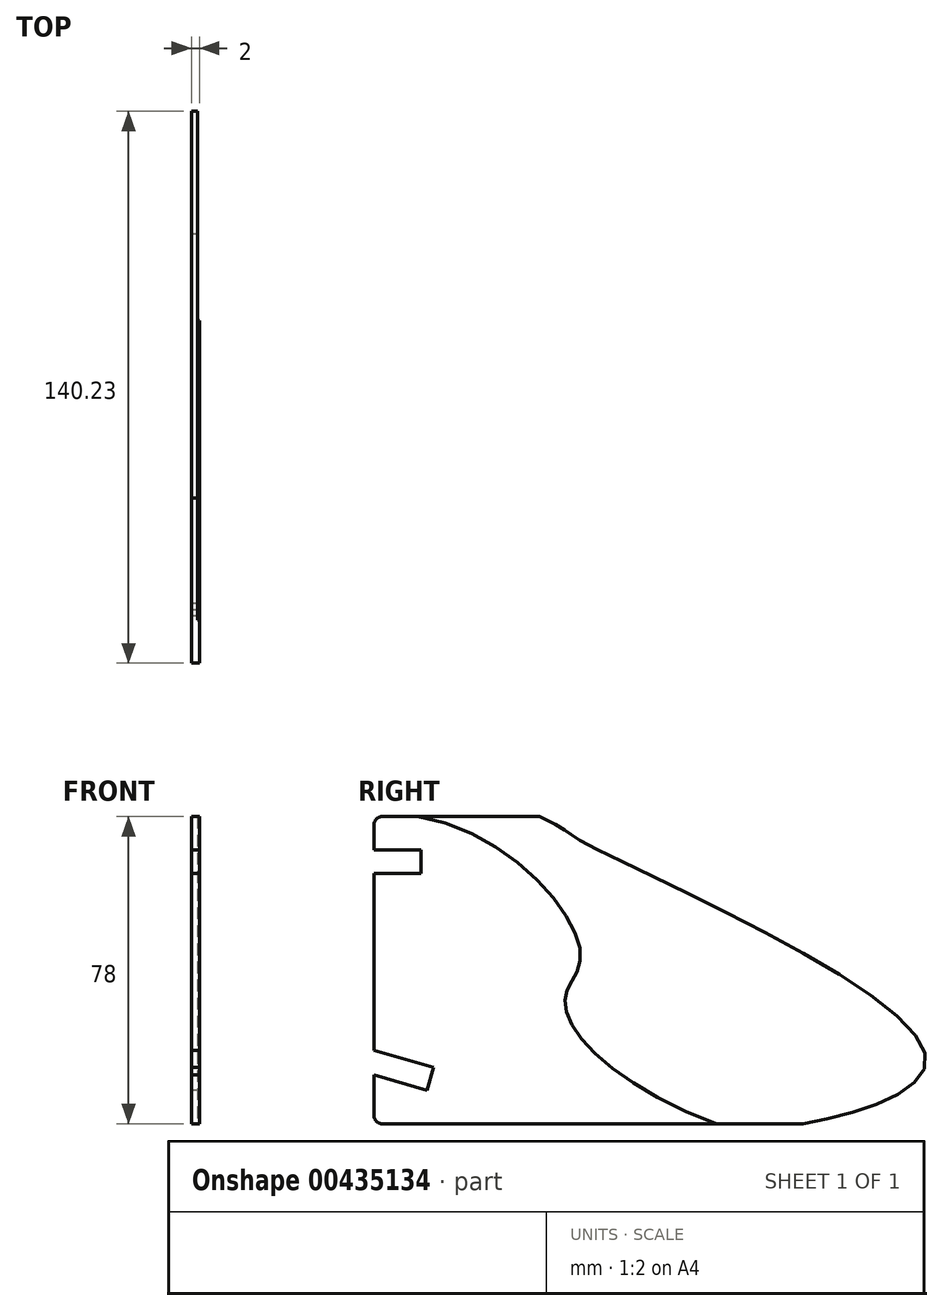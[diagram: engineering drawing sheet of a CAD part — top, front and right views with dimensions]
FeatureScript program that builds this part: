
annotation { "Feature Type Name" : "Feature", "Feature Type Description" : "" }
export const myFeature = defineFeature(function(context is Context, id is Id, definition is map)
    precondition{}
    {
        {
            var Q0;
            Q0=qCreatedBy(makeId("Right.planeOp"),FACE);
            var sketch = newSketch(context, id + "F0", { "sketchPlane" : qUnion([Q0])});
            skLineSegment(sketch, "E0", {"start": v(2, 78) * mm, "end": v(42, 78) * mm});
            skLineSegment(sketch, "E1", {"start": v(2, 0) * mm, "end": v(109, 0) * mm});
            skLineSegment(sketch, "E2", {"start": v(0, 76) * mm, "end": v(0, 69.6) * mm});
            skLineSegment(sketch, "E3", {"start": v(0, 69.6) * mm, "end": v(12, 69.6) * mm});
            skLineSegment(sketch, "E4", {"start": v(12, 69.6) * mm, "end": v(12, 63.6) * mm});
            skLineSegment(sketch, "E5", {"start": v(12, 63.6) * mm, "end": v(0, 63.6) * mm});
            skLineSegment(sketch, "E6", {"start": v(0, 63.6) * mm, "end": v(0, 18.6) * mm});
            skLineSegment(sketch, "E7", {"start": v(0, 18.6) * mm, "end": v(15.11, 14.26) * mm});
            skLineSegment(sketch, "E8", {"start": v(15.11, 14.26) * mm, "end": v(13.46, 8.5) * mm});
            skLineSegment(sketch, "E9", {"start": v(13.46, 8.5) * mm, "end": v(0, 12.35) * mm});
            skLineSegment(sketch, "E10", {"start": v(0, 12.35) * mm, "end": v(0, 2) * mm});
            skPoint(sketch, "E11.visualSharp", {"position": v(0, 78) * mm});
            skArc(sketch, "E11.filletArc", {"start": v(2, 78) * mm, "mid": v(0.59, 77.41) * mm, "end": v(0, 76) * mm});
            skPoint(sketch, "E12.visualSharp", {"position": v(0, 0) * mm});
            skArc(sketch, "E12.filletArc", {"start": v(0, 2) * mm, "mid": v(0.59, 0.59) * mm, "end": v(2, 0) * mm});
            skFitSpline(sketch, "E13", {"points": [v(42, 78) * mm, v(52.9, 71.65) * mm, v(140, 18) * mm, v(109, 0) * mm], "startDerivative": vector(128.82, -58.6) * mm, "endDerivative": vector(-133.84, -23.06) * mm});
            skSolve(sketch);
        }
        {
            var Q0;
            Q0 = qSketchRegion(id + "F0", true);
            extrude(context, id + "F1", {"entities" : qUnion([Q0]), "depth" : 1.5 * mm});
        }
        {
            var Q0;
            Q0=makeQuery(id+"F1.opExtrude","CAP_FACE",FACE,{"disambiguationData":[OSD([sQuery(id+"F0.wireOp",EDGE,"E0"),sQuery(id+"F0.wireOp",EDGE,"E1"),sQuery(id+"F0.wireOp",EDGE,"E2"),sQuery(id+"F0.wireOp",EDGE,"E3"),sQuery(id+"F0.wireOp",EDGE,"E4"),sQuery(id+"F0.wireOp",EDGE,"E5"),sQuery(id+"F0.wireOp",EDGE,"E6"),sQuery(id+"F0.wireOp",EDGE,"E7"),sQuery(id+"F0.wireOp",EDGE,"E8"),sQuery(id+"F0.wireOp",EDGE,"E9"),sQuery(id+"F0.wireOp",EDGE,"E10"),sQuery(id+"F0.wireOp",EDGE,"E11.filletArc"),sQuery(id+"F0.wireOp",EDGE,"E12.filletArc"),sQuery(id+"F0.wireOp",EDGE,"E13")])],"isStart":false});
            var sketch = newSketch(context, id + "F2", { "sketchPlane" : qUnion([Q0])});
            skSolve(sketch);
        }
        {
            var Q0;
            Q0=makeQuery(id+"F2.imprint","IMPRINT",FACE,{"disambiguationData":[TD([[makeQuery(id+"F2.imprint","IMPRINT",EDGE,{"derivedFrom":makeQuery(id+"F1.opExtrude","CAP_EDGE",EDGE,{"disambiguationData":[OSD([sQuery(id+"F0.wireOp",EDGE,"E0")])],"isStart":false})}),-1.0]])]});
            var sketch = newSketch(context, id + "F3", { "sketchPlane" : qUnion([Q0])});
            skLineSegment(sketch, "E14", {"start": v(11, 0) * mm, "end": v(11, 78) * mm, "construction": true});
            skFitSpline(sketch, "E15", {"points": [v(11, 78) * mm, v(52.5, 43) * mm, v(48.5, 31.5) * mm, v(87, 0) * mm], "startDerivative": vector(166.3, -24.45) * mm, "endDerivative": vector(190.57, -69.04) * mm});
            skLineSegment(sketch, "E16", {"start": v(11, 78) * mm, "end": v(2, 78) * mm});
            skLineSegment(sketch, "E17", {"start": v(0, 76) * mm, "end": v(0, 2) * mm});
            skLineSegment(sketch, "E18", {"start": v(2, 0) * mm, "end": v(87, 0) * mm});
            skPoint(sketch, "E19.visualSharp", {"position": v(0, 78) * mm});
            skArc(sketch, "E19.filletArc", {"start": v(2, 78) * mm, "mid": v(0.59, 77.41) * mm, "end": v(0, 76) * mm});
            skPoint(sketch, "E20.visualSharp", {"position": v(0, 0) * mm});
            skArc(sketch, "E20.filletArc", {"start": v(0, 2) * mm, "mid": v(0.59, 0.59) * mm, "end": v(2, 0) * mm});
            skSolve(sketch);
        }
        {
            var Q0;
            Q0 = qSketchRegion(id + "F3", true);
            extrude(context, id + "F4", {"entities" : qUnion([Q0]), "operationType" : NewBodyOperationType.ADD, "depth" : .5 * mm});
        }
        {
            var Q0;
            Q0=makeQuery(id+"F1.opExtrude","CAP_FACE",FACE,{"disambiguationData":[OSD([sQuery(id+"F0.wireOp",EDGE,"E0"),sQuery(id+"F0.wireOp",EDGE,"E1"),sQuery(id+"F0.wireOp",EDGE,"E2"),sQuery(id+"F0.wireOp",EDGE,"E3"),sQuery(id+"F0.wireOp",EDGE,"E4"),sQuery(id+"F0.wireOp",EDGE,"E5"),sQuery(id+"F0.wireOp",EDGE,"E6"),sQuery(id+"F0.wireOp",EDGE,"E7"),sQuery(id+"F0.wireOp",EDGE,"E8"),sQuery(id+"F0.wireOp",EDGE,"E9"),sQuery(id+"F0.wireOp",EDGE,"E10"),sQuery(id+"F0.wireOp",EDGE,"E11.filletArc"),sQuery(id+"F0.wireOp",EDGE,"E12.filletArc"),sQuery(id+"F0.wireOp",EDGE,"E13")])],"isStart":true});
            var sketch = newSketch(context, id + "F5", { "sketchPlane" : qUnion([Q0])});
            skLineSegment(sketch, "E21.bottom", {"start": v(-12, 69.6) * mm, "end": v(0, 69.6) * mm});
            skLineSegment(sketch, "E21.top", {"start": v(-12, 63.6) * mm, "end": v(0, 63.6) * mm});
            skLineSegment(sketch, "E21.left", {"start": v(-12, 69.6) * mm, "end": v(-12, 63.6) * mm});
            skLineSegment(sketch, "E21.right", {"start": v(0, 69.6) * mm, "end": v(0, 63.6) * mm});
            skLineSegment(sketch, "E22", {"start": v(0, 18.6) * mm, "end": v(-15.11, 14.26) * mm});
            skLineSegment(sketch, "E23", {"start": v(-15.11, 14.26) * mm, "end": v(-13.46, 8.5) * mm});
            skLineSegment(sketch, "E24", {"start": v(-13.46, 8.5) * mm, "end": v(0, 12.35) * mm});
            skLineSegment(sketch, "E25", {"start": v(0, 12.35) * mm, "end": v(0, 18.6) * mm});
            skSolve(sketch);
        }
        {
            var Q0;
            Q0 = qSketchRegion(id + "F5", true);
            extrude(context, id + "F6", {"entities" : qUnion([Q0]), "operationType" : NewBodyOperationType.REMOVE, "oppositeDirection" : true, "depth" : 25 * mm});
        }
    });
